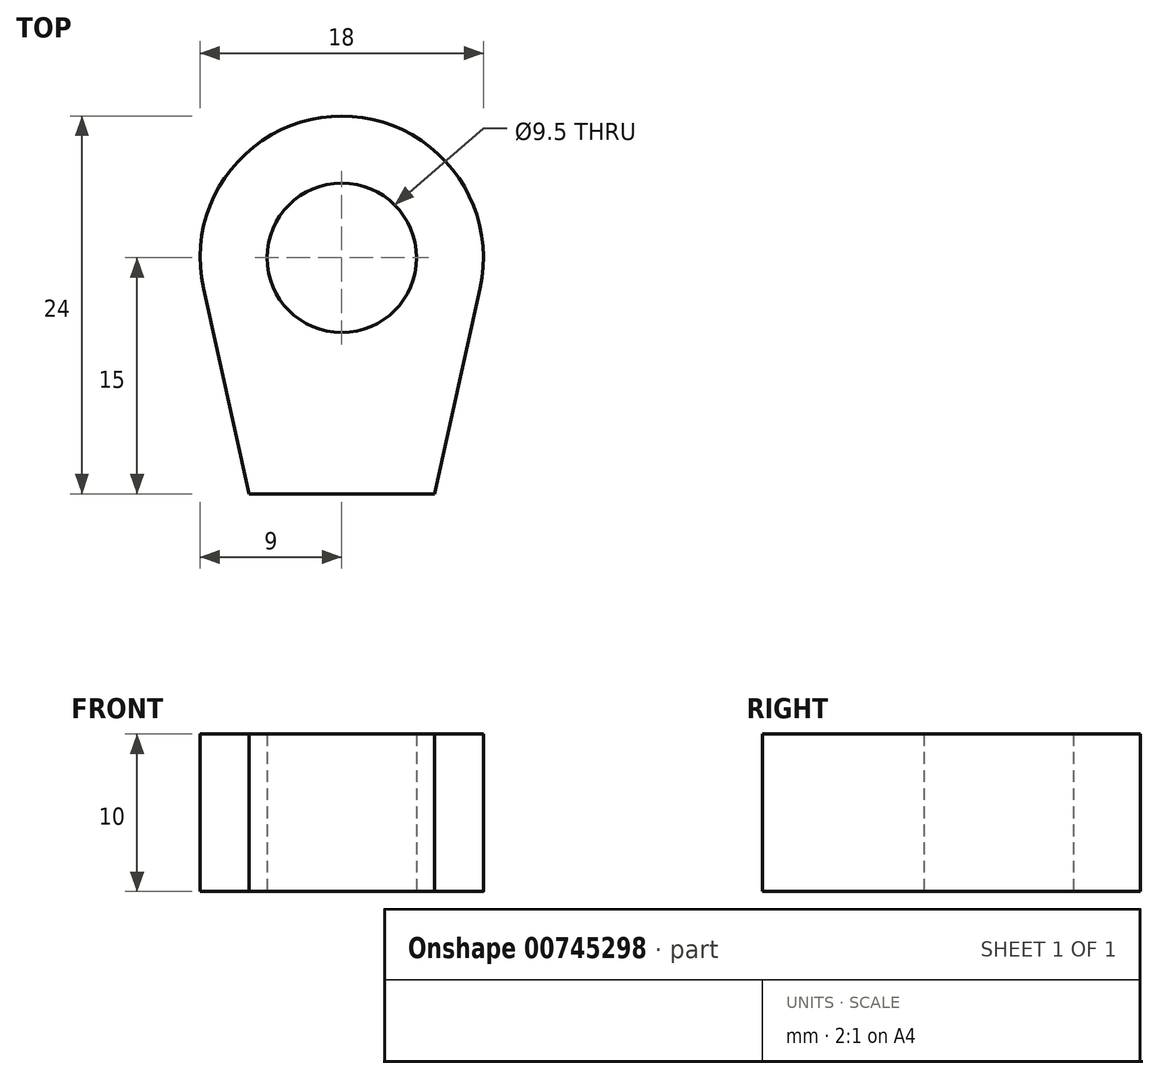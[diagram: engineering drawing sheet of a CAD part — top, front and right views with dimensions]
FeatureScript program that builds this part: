
annotation { "Feature Type Name" : "Feature", "Feature Type Description" : "" }
export const myFeature = defineFeature(function(context is Context, id is Id, definition is map)
    precondition{}
    {
        {
            var Q0;
            Q0=qCreatedBy(makeId("Top.planeOp"),FACE);
            var sketch = newSketch(context, id + "F0", { "sketchPlane" : qUnion([Q0])});
            skArc(sketch, "E0", {"start": v(0, 9) * mm, "mid": v(-7.02, 5.63) * mm, "end": v(-8.79, -1.95) * mm});
            skCircle(sketch, "E1", {"center": v(0, 0) * mm, "radius": 4.75 * mm});
            skLineSegment(sketch, "E2", {"start": v(-5.9, -15) * mm, "end": v(0, -15) * mm});
            skLineSegment(sketch, "E3", {"start": v(0, -15) * mm, "end": v(0, 9) * mm, "construction": true});
            skLineSegment(sketch, "E4", {"start": v(-8.79, -1.95) * mm, "end": v(-5.9, -15) * mm});
            skLineSegment(sketch, "E5.MirrorCS", {"start": v(5.9, -15) * mm, "end": v(0, -15) * mm});
            skArc(sketch, "E6.MirrorCS", {"start": v(0, 9) * mm, "mid": v(7.02, 5.63) * mm, "end": v(8.79, -1.95) * mm});
            skLineSegment(sketch, "E7.MirrorCS", {"start": v(8.79, -1.95) * mm, "end": v(5.9, -15) * mm});
            skSolve(sketch);
        }
        {
            var Q0;
            Q0 = qSketchRegion(id + "F0", true);
            extrude(context, id + "F1", {"entities" : qUnion([Q0]), "depth" : 10 * mm, "offsetDistance" : 25 * mm});
        }
    });
